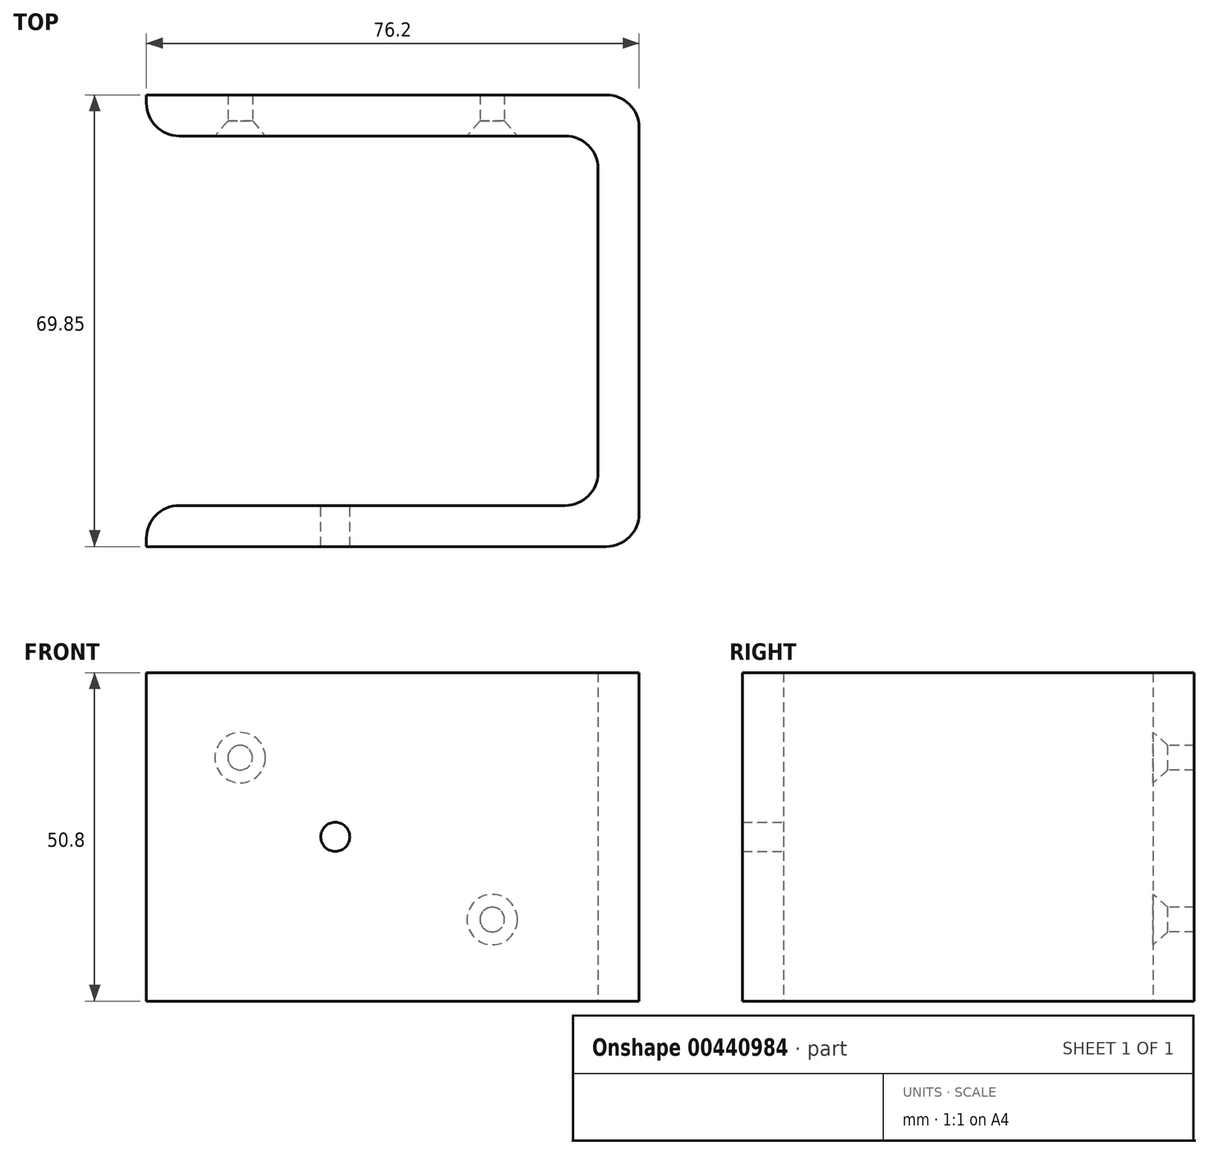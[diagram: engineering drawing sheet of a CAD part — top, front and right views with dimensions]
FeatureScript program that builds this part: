
annotation { "Feature Type Name" : "Feature", "Feature Type Description" : "" }
export const myFeature = defineFeature(function(context is Context, id is Id, definition is map)
    precondition{}
    {
        {
            var Q0;
            Q0=qCreatedBy(makeId("Top.planeOp"),FACE);
            var sketch = newSketch(context, id + "F0", { "sketchPlane" : qUnion([Q0])});
            skLineSegment(sketch, "E0", {"start": v(-35.86, 0) * mm, "end": v(34, 0) * mm});
            skLineSegment(sketch, "E1", {"start": v(34, 0) * mm, "end": v(34, 57.15) * mm});
            skLineSegment(sketch, "E2", {"start": v(34, 57.15) * mm, "end": v(-35.86, 57.15) * mm});
            skLineSegment(sketch, "E3", {"start": v(-35.86, 57.15) * mm, "end": v(-35.86, 63.5) * mm});
            skLineSegment(sketch, "E4", {"start": v(-35.86, 63.5) * mm, "end": v(40.34, 63.5) * mm});
            skLineSegment(sketch, "E5", {"start": v(40.34, 63.5) * mm, "end": v(40.34, -6.35) * mm});
            skLineSegment(sketch, "E6", {"start": v(40.34, -6.35) * mm, "end": v(-35.86, -6.35) * mm});
            skLineSegment(sketch, "E7", {"start": v(-35.86, -6.35) * mm, "end": v(-35.86, 0) * mm});
            skSolve(sketch);
        }
        {
            var Q0;
            Q0=makeQuery(id+"F0.imprint","IMPRINT",FACE,{"disambiguationData":[TD([[makeQuery(id+"F0.imprint","IMPRINT",EDGE,{"derivedFrom":sQuery(id+"F0.wireOp",EDGE,"E0")}),-1.0]])]});
            extrude(context, id + "F1", {"entities" : qUnion([Q0]), "depth" : 50.8 * mm});
        }
        {
            var Q0;
            Q0=makeQuery(id+"F1.opExtrude","SWEPT_FACE",FACE,{"disambiguationData":[OSD([sQuery(id+"F0.wireOp",EDGE,"E2")])]});
            var sketch = newSketch(context, id + "F2", { "sketchPlane" : qUnion([Q0])});
            skPoint(sketch, "E8", {"position": v(-21.36, 37.64) * mm});
            skPoint(sketch, "E9", {"position": v(17.63, 12.61) * mm});
            skSolve(sketch);
        }
        {
            var Q0;
            Q0=sQuery(id+"F2.wireOp",VERTEX,"E8");
            var Q1;
            Q1=sQuery(id+"F2.wireOp",VERTEX,"E9");
            var Q2;
            Q2=makeQuery(id+"F1.opExtrude","SWEPT_BODY",BODY,{"disambiguationData":[OSD([sQuery(id+"F0.wireOp",EDGE,"E0"),sQuery(id+"F0.wireOp",EDGE,"E1"),sQuery(id+"F0.wireOp",EDGE,"E2"),sQuery(id+"F0.wireOp",EDGE,"E3"),sQuery(id+"F0.wireOp",EDGE,"E4"),sQuery(id+"F0.wireOp",EDGE,"E5"),sQuery(id+"F0.wireOp",EDGE,"E6"),sQuery(id+"F0.wireOp",EDGE,"E7")])]});
            hole(context, id + "F3", {"style" : HoleStyle.C_SINK, "endStyle" : HoleEndStyle.THROUGH, "standardTappedOrClearance" : lookupTablePath({ "standard" : "ANSI", "fit" : "Normal (ASME)", "size" : "#6", "type" : "Clearance" }), "standardBlindInLast" : lookupTablePath({ "fit" : "Free", "standard" : "ANSI", "size" : "#6", "type" : "Clearance" }), "holeDiameter" : 3.8 * mm, "cSinkDiameter" : 7.8 * mm, "cSinkAngle" : 82 * degree, "isTappedThrough" : true, "tappedDepth" : 12.7 * mm, "tapClearance" : 3, "startFromSketch" : true, "locations" : qUnion([Q0, Q1]), "scope" : qUnion([Q2])});
        }
        {
            var Q0;
            Q0=qCreatedBy(makeId("Front.planeOp"),FACE);
            var sketch = newSketch(context, id + "F4", { "sketchPlane" : qUnion([Q0])});
            skPoint(sketch, "E10", {"position": v(-6.65, 25.4) * mm});
            skSolve(sketch);
        }
        {
            var Q0;
            Q0=makeQuery(id+"F1.opExtrude","SWEPT_EDGE",EDGE,{"disambiguationData":[OSD([sQuery(id+"F0.wireOp",EDGE,"E1"),sQuery(id+"F0.wireOp",EDGE,"E2")])]});
            var Q1;
            Q1=makeQuery(id+"F1.opExtrude","SWEPT_EDGE",EDGE,{"disambiguationData":[OSD([sQuery(id+"F0.wireOp",EDGE,"E0"),sQuery(id+"F0.wireOp",EDGE,"E1")])]});
            var Q2;
            Q2=makeQuery(id+"F1.opExtrude","SWEPT_EDGE",EDGE,{"disambiguationData":[OSD([sQuery(id+"F0.wireOp",EDGE,"E4"),sQuery(id+"F0.wireOp",EDGE,"E5")])]});
            var Q3;
            Q3=makeQuery(id+"F1.opExtrude","SWEPT_EDGE",EDGE,{"disambiguationData":[OSD([sQuery(id+"F0.wireOp",EDGE,"E5"),sQuery(id+"F0.wireOp",EDGE,"E6")])]});
            var Q4;
            Q4=makeQuery(id+"F1.opExtrude","SWEPT_EDGE",EDGE,{"disambiguationData":[OSD([sQuery(id+"F0.wireOp",EDGE,"E2"),sQuery(id+"F0.wireOp",EDGE,"E3")])]});
            var Q5;
            Q5=makeQuery(id+"F1.opExtrude","SWEPT_EDGE",EDGE,{"disambiguationData":[OSD([sQuery(id+"F0.wireOp",EDGE,"E0"),sQuery(id+"F0.wireOp",EDGE,"E7")])]});
            fillet(context, id + "F5", {"entities" : qUnion([Q0, Q1, Q2, Q3, Q4, Q5]), "radius" : 5.08 * mm, "tangentPropagation" : true, "allowEdgeOverflow" : false});
        }
        {
            var Q0;
            Q0=sQuery(id+"F4.wireOp",VERTEX,"E10");
            var Q1;
            Q1=makeQuery(id+"F1.opExtrude","SWEPT_BODY",BODY,{"disambiguationData":[OSD([sQuery(id+"F0.wireOp",EDGE,"E0"),sQuery(id+"F0.wireOp",EDGE,"E1"),sQuery(id+"F0.wireOp",EDGE,"E2"),sQuery(id+"F0.wireOp",EDGE,"E3"),sQuery(id+"F0.wireOp",EDGE,"E4"),sQuery(id+"F0.wireOp",EDGE,"E5"),sQuery(id+"F0.wireOp",EDGE,"E6"),sQuery(id+"F0.wireOp",EDGE,"E7")])]});
            hole(context, id + "F6", {"style" : HoleStyle.SIMPLE, "endStyle" : HoleEndStyle.THROUGH, "oppositeDirection" : true, "standardTappedOrClearance" : lookupTablePath({ "standard" : "ANSI", "fit" : "Normal (ASME)", "size" : "#8", "type" : "Clearance" }), "standardBlindInLast" : lookupTablePath({ "fit" : "Free", "standard" : "ANSI", "size" : "#8", "type" : "Clearance" }), "holeDiameter" : 4.5 * mm, "isTappedThrough" : true, "tappedDepth" : 12.7 * mm, "tapClearance" : 3, "startFromSketch" : true, "locations" : qUnion([Q0]), "scope" : qUnion([Q1])});
        }
    });
